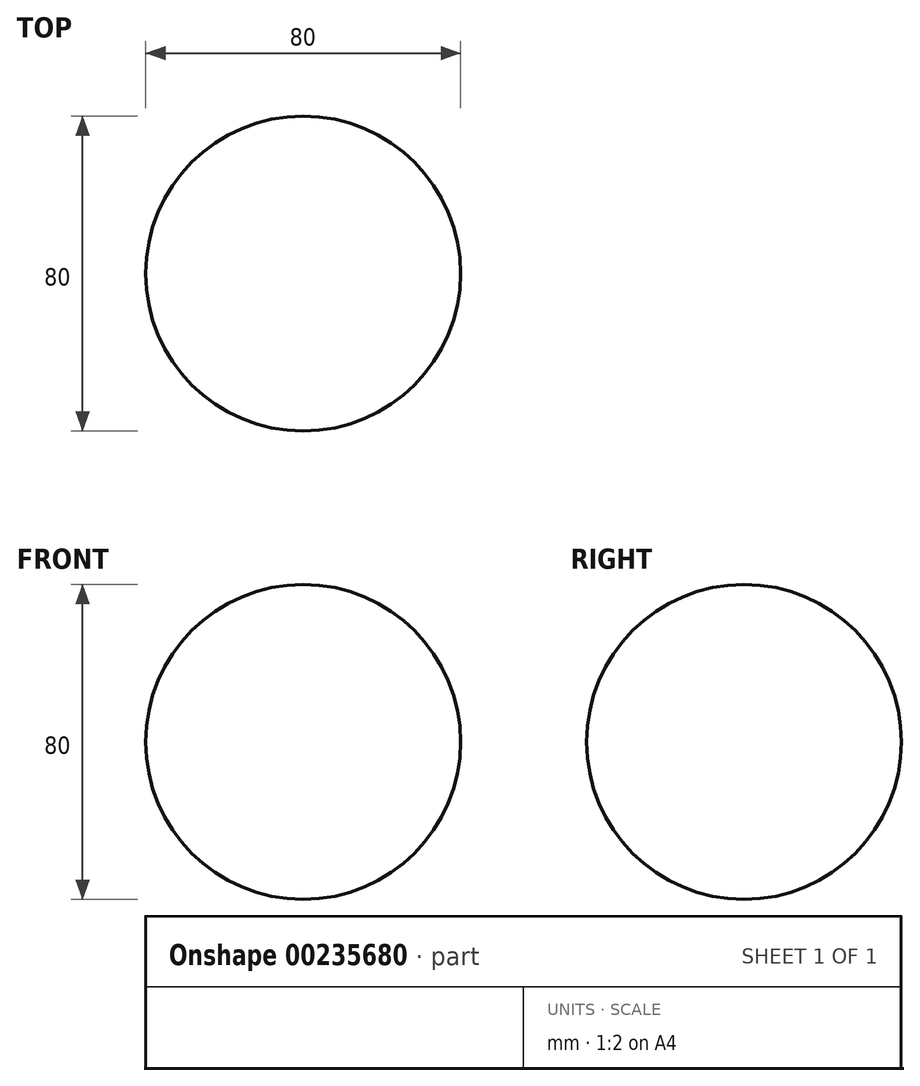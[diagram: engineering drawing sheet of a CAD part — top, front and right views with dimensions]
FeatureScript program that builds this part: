
annotation { "Feature Type Name" : "Feature", "Feature Type Description" : "" }
export const myFeature = defineFeature(function(context is Context, id is Id, definition is map)
    precondition{}
    {
        {
            var Q0;
            Q0=qCreatedBy(makeId("Front.planeOp"),FACE);
            var sketch = newSketch(context, id + "F0", { "sketchPlane" : qUnion([Q0])});
            skArc(sketch, "E0", {"start": v(0, 40) * mm, "mid": v(-40, 0) * mm, "end": v(0, -40) * mm});
            skLineSegment(sketch, "E1", {"start": v(0, 40) * mm, "end": v(0, -40) * mm});
            skSolve(sketch);
        }
        {
            var Q0;
            Q0=makeQuery(id+"F0.imprint","IMPRINT",FACE,{"disambiguationData":[TD([[makeQuery(id+"F0.imprint","IMPRINT",EDGE,{"derivedFrom":sQuery(id+"F0.wireOp",EDGE,"E0")}),1.0]])]});
            var Q1;
            Q1=sQuery(id+"F0.wireOp",EDGE,"E1");
            revolve(context, id + "F1", {"entities" : qUnion([Q0]), "axis" : qUnion([Q1]), "revolveType" : RevolveType.FULL});
        }
    });
